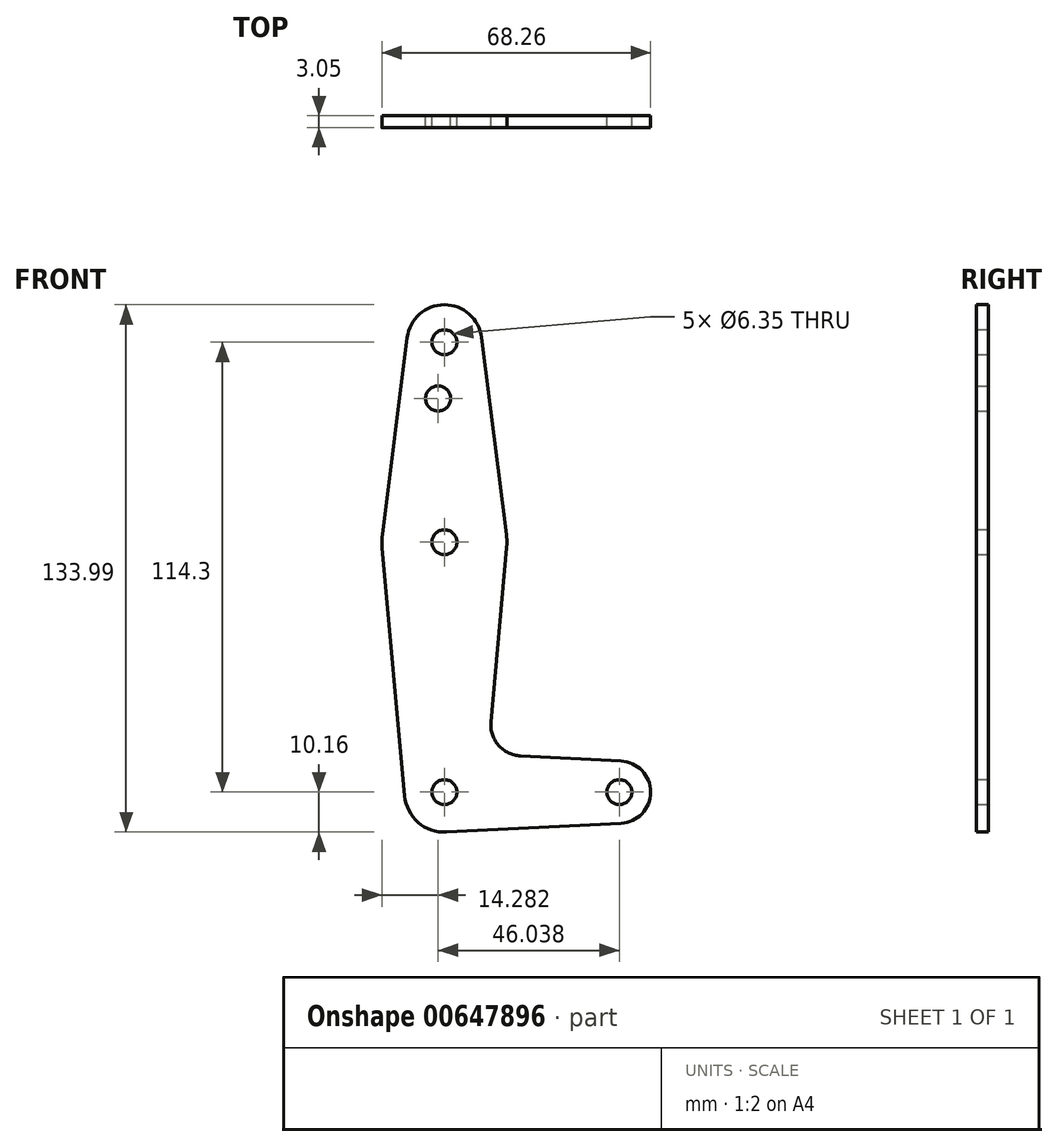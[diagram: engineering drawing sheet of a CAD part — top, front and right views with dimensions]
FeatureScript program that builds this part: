
annotation { "Feature Type Name" : "Feature", "Feature Type Description" : "" }
export const myFeature = defineFeature(function(context is Context, id is Id, definition is map)
    precondition{}
    {
        {
            var Q0;
            Q0=qCreatedBy(makeId("Front.planeOp"),FACE);
            var sketch = newSketch(context, id + "F0", { "sketchPlane" : qUnion([Q0])});
            skCircle(sketch, "E0", {"center": v(0, 0) * mm, "radius": 10.16 * mm});
            skLineSegment(sketch, "E1", {"start": v(0, 0) * mm, "end": v(0, 114.3) * mm, "construction": true});
            skCircle(sketch, "E2", {"center": v(0, 63.5) * mm, "radius": 15.88 * mm});
            skCircle(sketch, "E3", {"center": v(0, 114.3) * mm, "radius": 9.53 * mm});
            skLineSegment(sketch, "E4", {"start": v(0, 0) * mm, "end": v(44.45, 0) * mm, "construction": true});
            skCircle(sketch, "E5", {"center": v(44.45, 0) * mm, "radius": 7.94 * mm});
            skLineSegment(sketch, "E6", {"start": v(-9.45, 115.5) * mm, "end": v(-15.75, 65.48) * mm});
            skLineSegment(sketch, "E7", {"start": v(9.45, 115.5) * mm, "end": v(15.75, 65.48) * mm});
            skLineSegment(sketch, "E8", {"start": v(15.81, 62.07) * mm, "end": v(11.81, 17.85) * mm});
            skLineSegment(sketch, "E9", {"start": v(19.34, 9.2) * mm, "end": v(44.84, 7.93) * mm});
            skLineSegment(sketch, "E10", {"start": v(0.5, -10.15) * mm, "end": v(44.85, -7.93) * mm});
            skLineSegment(sketch, "E11", {"start": v(-10.12, -0.91) * mm, "end": v(-15.81, 62.07) * mm});
            skCircle(sketch, "E12", {"center": v(0, 114.3) * mm, "radius": 3.18 * mm});
            skCircle(sketch, "E13", {"center": v(0, 63.5) * mm, "radius": 3.18 * mm});
            skCircle(sketch, "E14", {"center": v(-1.59, 100.03) * mm, "radius": 3.18 * mm});
            skCircle(sketch, "E15", {"center": v(0, 0) * mm, "radius": 3.18 * mm});
            skCircle(sketch, "E16", {"center": v(44.45, 0) * mm, "radius": 3.18 * mm});
            skArc(sketch, "E17.filletArc", {"start": v(11.81, 17.85) * mm, "mid": v(13.73, 11.92) * mm, "end": v(19.34, 9.2) * mm});
            skSolve(sketch);
        }
        {
            var Q0;
            Q0 = qSketchRegion(id + "F0", true);
            extrude(context, id + "F1", {"entities" : qUnion([Q0]), "depth" : 3.05 * mm, "offsetDistance" : 25.4 * mm});
        }
    });
